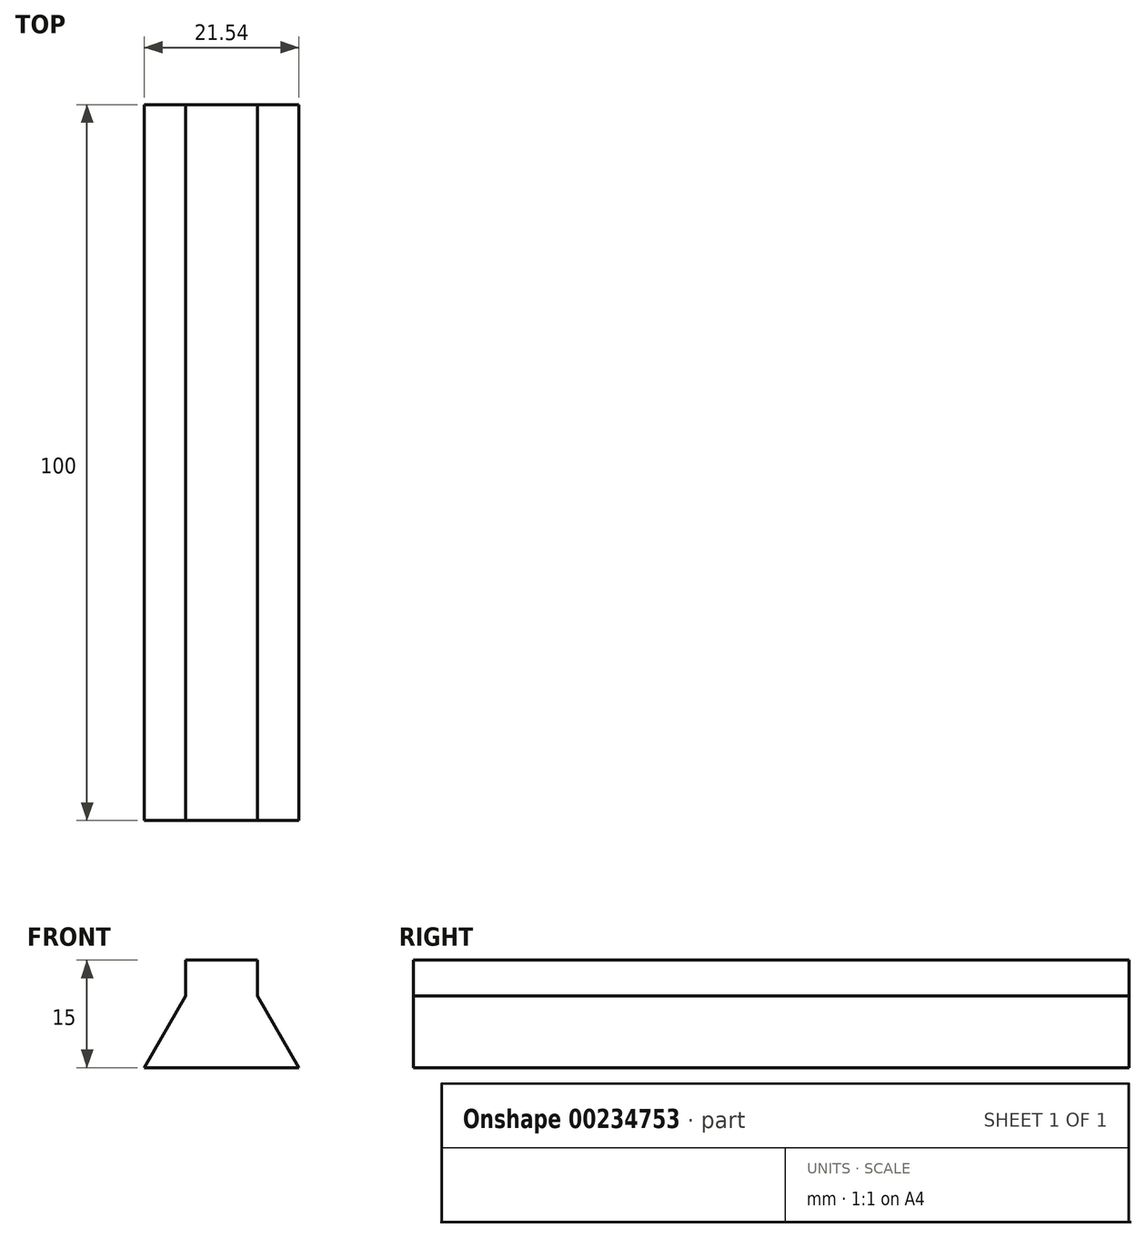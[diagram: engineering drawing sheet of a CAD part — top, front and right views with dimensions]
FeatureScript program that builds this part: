
annotation { "Feature Type Name" : "Feature", "Feature Type Description" : "" }
export const myFeature = defineFeature(function(context is Context, id is Id, definition is map)
    precondition{}
    {
        {
            var Q0;
            Q0=qCreatedBy(makeId("Front.planeOp"),FACE);
            cPlane(context, id + "F0", {"entities" : qUnion([Q0]), "cplaneType" : CPlaneType.OFFSET, "offset" : 50 * mm, "width" : 150 * mm, "height" : 150 * mm});
        }
        {
            var Q0;
            Q0=qCreatedBy(id+"F0.planeOp",FACE);
            var sketch = newSketch(context, id + "F1", { "sketchPlane" : qUnion([Q0])});
            skLineSegment(sketch, "E0", {"start": v(5, 0) * mm, "end": v(10.77, -10) * mm});
            skLineSegment(sketch, "E1", {"start": v(10.77, -10) * mm, "end": v(-10.77, -10) * mm});
            skLineSegment(sketch, "E2", {"start": v(-10.77, -10) * mm, "end": v(-5, 0) * mm});
            skLineSegment(sketch, "E3", {"start": v(-5, 0) * mm, "end": v(-5, 5) * mm});
            skLineSegment(sketch, "E4", {"start": v(-5, 5) * mm, "end": v(5, 5) * mm});
            skLineSegment(sketch, "E5", {"start": v(5, 5) * mm, "end": v(5, 0) * mm});
            skSolve(sketch);
        }
        {
            var Q0;
            Q0 = qSketchRegion(id + "F1", true);
            extrude(context, id + "F2", {"entities" : qUnion([Q0]), "oppositeDirection" : true, "depth" : 100 * mm});
        }
    });
